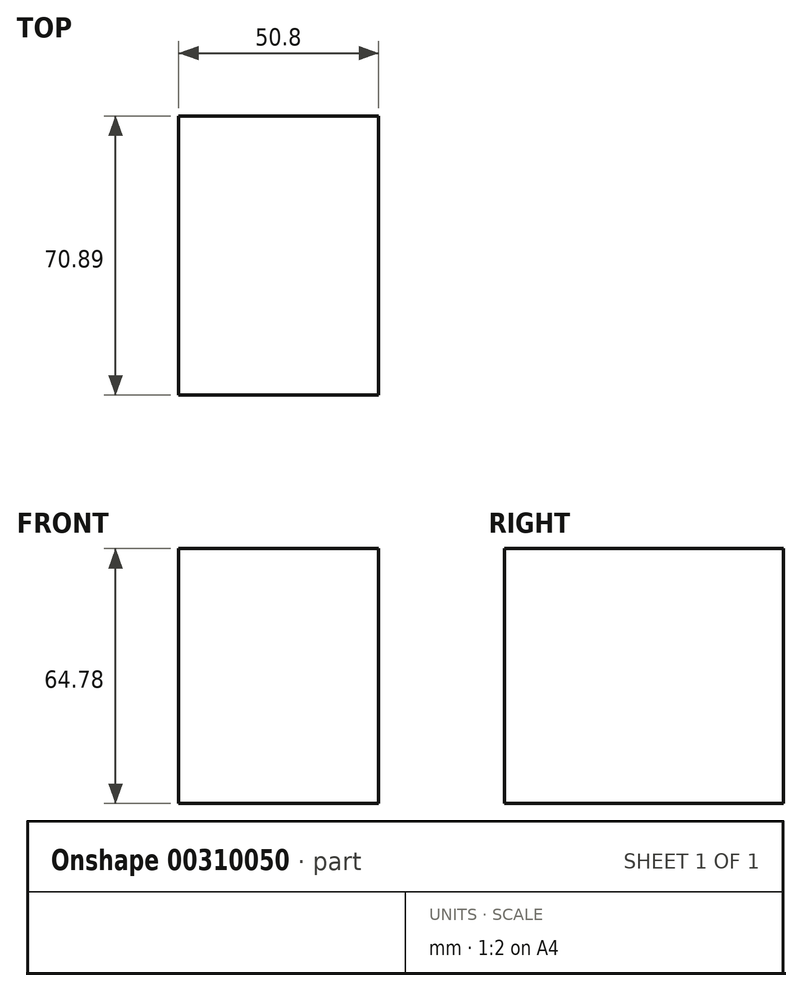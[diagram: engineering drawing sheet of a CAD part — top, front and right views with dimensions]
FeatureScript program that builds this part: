
annotation { "Feature Type Name" : "Feature", "Feature Type Description" : "" }
export const myFeature = defineFeature(function(context is Context, id is Id, definition is map)
    precondition{}
    {
        {
            var Q0;
            Q0=qCreatedBy(makeId("Right.planeOp"),FACE);
            var sketch = newSketch(context, id + "F0", { "sketchPlane" : qUnion([Q0])});
            skLineSegment(sketch, "E0.bottom", {"start": v(0, 0) * mm, "end": v(70.9, 0) * mm});
            skLineSegment(sketch, "E0.top", {"start": v(0, -64.78) * mm, "end": v(70.9, -64.78) * mm});
            skLineSegment(sketch, "E0.left", {"start": v(0, 0) * mm, "end": v(0, -64.78) * mm});
            skLineSegment(sketch, "E0.right", {"start": v(70.9, 0) * mm, "end": v(70.9, -64.78) * mm});
            skSolve(sketch);
        }
        {
            var Q0;
            Q0=makeQuery(id+"F0.imprint","IMPRINT",FACE,{"disambiguationData":[TD([[makeQuery(id+"F0.imprint","IMPRINT",EDGE,{"derivedFrom":sQuery(id+"F0.wireOp",EDGE,"E0.bottom")}),-1.0]])]});
            extrude(context, id + "F1", {"entities" : qUnion([Q0]), "depth" : 50.8 * mm});
        }
    });
